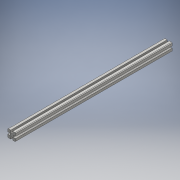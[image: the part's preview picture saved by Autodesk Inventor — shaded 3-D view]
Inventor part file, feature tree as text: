
AUTODESK INVENTOR PART (.ipt)
format: ipt  version: 2016 (Build 200138000, 138)  size: 120,320 bytes
history: native  units: mm
features: extrude x1, sketch x1
ambient origin geometry x8: Origin, YZ Plane, XZ Plane, XY Plane, X Axis, Y Axis, Z Axis, Center Point
bodies: Solid1 (feature_tree)
feature tree (2):
  extrude  "Extrusion1"  [1 undecoded]
  sketch  "Sketch1"  dims[d0=800.0mm d1=0.0mm]
note: 1 required parameter value undecoded (feature->parameter linkage not recoverable at this tier; creation-order binding heuristic only, values carry confidence <= 0.55)
